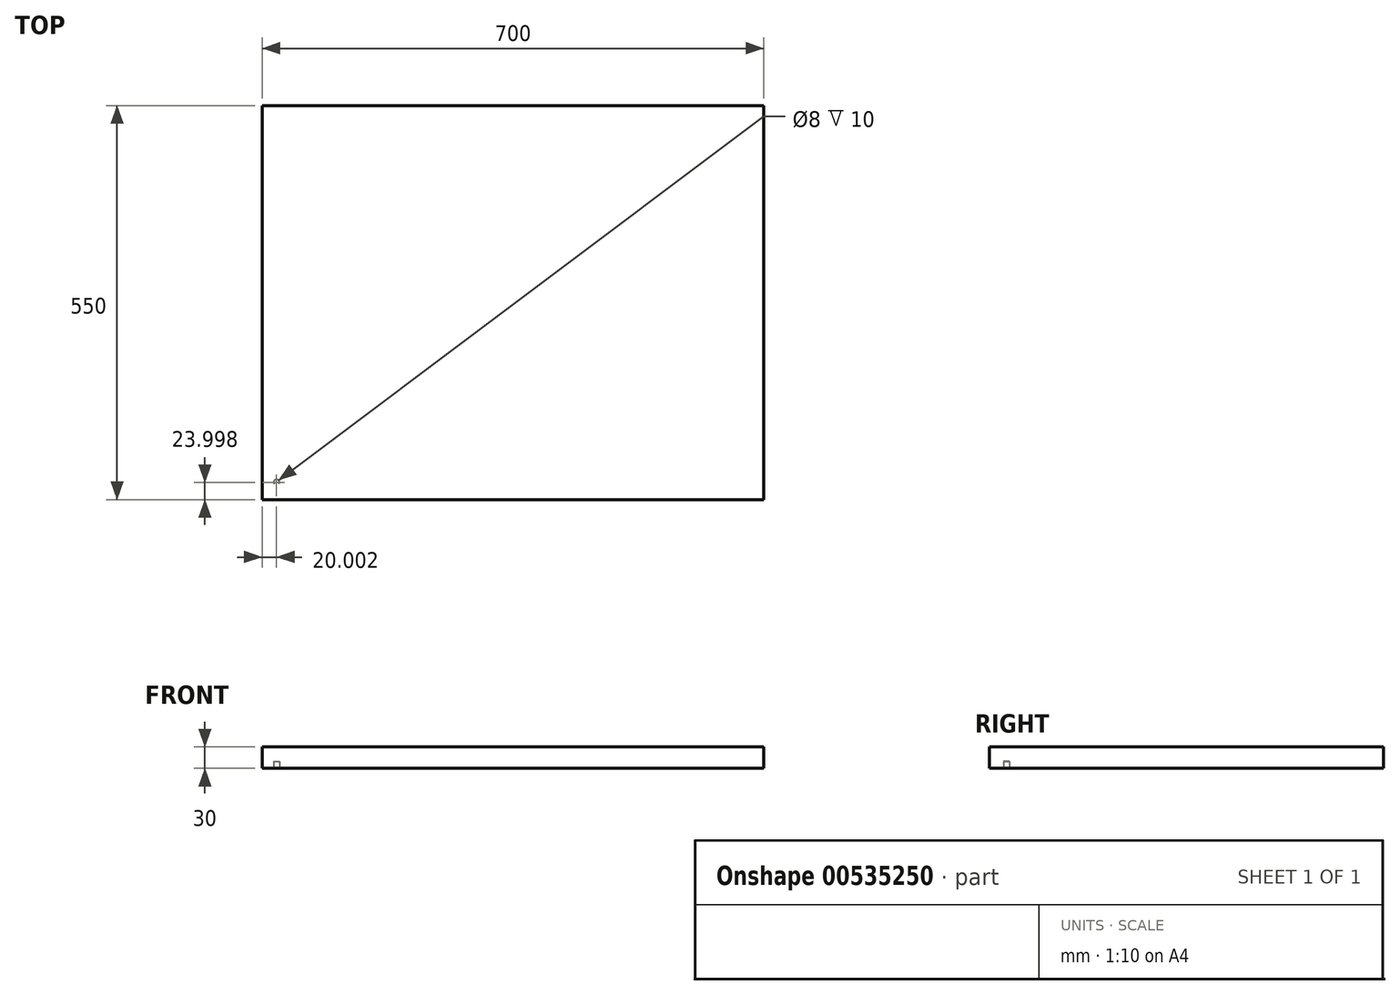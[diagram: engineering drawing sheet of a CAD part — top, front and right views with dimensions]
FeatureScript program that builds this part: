
annotation { "Feature Type Name" : "Feature", "Feature Type Description" : "" }
export const myFeature = defineFeature(function(context is Context, id is Id, definition is map)
    precondition{}
    {
        {
            var Q0;
            Q0=qCreatedBy(makeId("Top.planeOp"),FACE);
            var sketch = newSketch(context, id + "F0", { "sketchPlane" : qUnion([Q0])});
            skLineSegment(sketch, "E0.bottom", {"start": v(-571.2, 492.2) * mm, "end": v(128.8, 492.2) * mm});
            skLineSegment(sketch, "E0.top", {"start": v(-571.2, -57.8) * mm, "end": v(128.8, -57.8) * mm});
            skLineSegment(sketch, "E0.left", {"start": v(-571.2, 492.2) * mm, "end": v(-571.2, -57.8) * mm});
            skLineSegment(sketch, "E0.right", {"start": v(128.8, 492.2) * mm, "end": v(128.8, -57.8) * mm});
            skSolve(sketch);
        }
        {
            var Q0;
            Q0=makeQuery(id+"F0.imprint","IMPRINT",FACE,{"disambiguationData":[TD([[makeQuery(id+"F0.imprint","IMPRINT",EDGE,{"derivedFrom":sQuery(id+"F0.wireOp",EDGE,"E0.bottom")}),-1.0]])]});
            extrude(context, id + "F1", {"entities" : qUnion([Q0]), "depth" : 30 * mm, "offsetDistance" : 25 * mm});
        }
        {
            var Q0;
            Q0=makeQuery(id+"F1.opExtrude","CAP_FACE",FACE,{"disambiguationData":[OSD([sQuery(id+"F0.wireOp",EDGE,"E0.bottom"),sQuery(id+"F0.wireOp",EDGE,"E0.top"),sQuery(id+"F0.wireOp",EDGE,"E0.left"),sQuery(id+"F0.wireOp",EDGE,"E0.right")])],"isStart":true});
            var sketch = newSketch(context, id + "F2", { "sketchPlane" : qUnion([Q0])});
            skCircle(sketch, "E1", {"center": v(-551.2, 33.8) * mm, "radius": 4 * mm});
            skSolve(sketch);
        }
        {
            var Q0;
            Q0=makeQuery(id+"F2.imprint","IMPRINT",FACE,{"disambiguationData":[TD([[makeQuery(id+"F2.imprint","IMPRINT",EDGE,{"derivedFrom":sQuery(id+"F2.wireOp",EDGE,"E1")}),1.0]])]});
            extrude(context, id + "F3", {"entities" : qUnion([Q0]), "operationType" : NewBodyOperationType.REMOVE, "oppositeDirection" : true, "depth" : 10 * mm, "offsetDistance" : 25 * mm});
        }
    });
